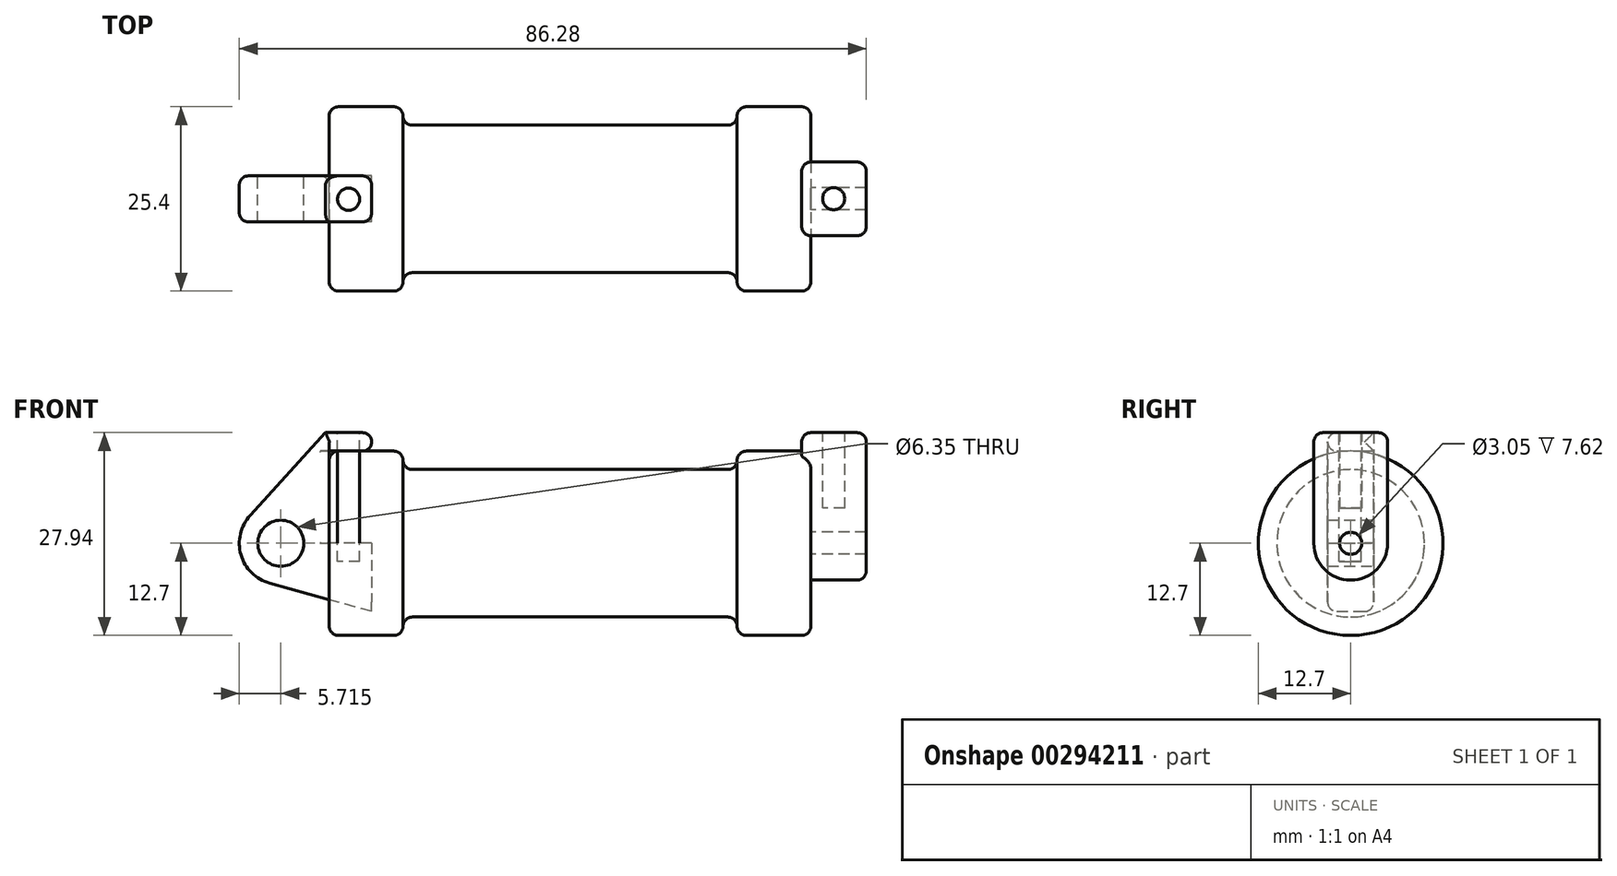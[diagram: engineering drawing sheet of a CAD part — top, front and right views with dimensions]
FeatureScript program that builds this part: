
annotation { "Feature Type Name" : "Feature", "Feature Type Description" : "" }
export const myFeature = defineFeature(function(context is Context, id is Id, definition is map)
    precondition{}
    {
        {
            var Q0;
            Q0=qCreatedBy(makeId("Front.planeOp"),FACE);
            var sketch = newSketch(context, id + "F0", { "sketchPlane" : qUnion([Q0])});
            skLineSegment(sketch, "E0", {"start": v(0, 0) * mm, "end": v(0, 12.7) * mm});
            skLineSegment(sketch, "E1", {"start": v(0, 12.7) * mm, "end": v(10.16, 12.7) * mm});
            skLineSegment(sketch, "E2", {"start": v(10.16, 12.7) * mm, "end": v(10.16, 10.16) * mm});
            skLineSegment(sketch, "E3", {"start": v(10.16, 10.16) * mm, "end": v(56.13, 10.16) * mm});
            skLineSegment(sketch, "E4", {"start": v(56.13, 10.16) * mm, "end": v(56.13, 12.7) * mm});
            skLineSegment(sketch, "E5", {"start": v(56.13, 12.7) * mm, "end": v(66.3, 12.7) * mm});
            skLineSegment(sketch, "E6", {"start": v(66.3, 12.7) * mm, "end": v(66.3, 0) * mm});
            skLineSegment(sketch, "E7", {"start": v(66.3, 0) * mm, "end": v(0, 0) * mm});
            skLineSegment(sketch, "E8", {"start": v(5.84, 15.24) * mm, "end": v(-0.5, 15.24) * mm});
            skLineSegment(sketch, "E9", {"start": v(-0.5, 15.24) * mm, "end": v(-10.88, 3.85) * mm});
            skLineSegment(sketch, "E10", {"start": v(0, 0) * mm, "end": v(-6.65, 0) * mm});
            skCircle(sketch, "E11", {"center": v(-6.65, 0) * mm, "radius": 5.72 * mm});
            skCircle(sketch, "E12", {"center": v(-6.65, 0) * mm, "radius": 3.18 * mm});
            skLineSegment(sketch, "E13", {"start": v(5.84, 15.24) * mm, "end": v(5.84, -9.4) * mm});
            skLineSegment(sketch, "E14", {"start": v(5.84, -9.4) * mm, "end": v(-8.18, -5.5) * mm});
            skSolve(sketch);
        }
        {
            var Q0;
            {var subQ5=sQuery(id+"F0.wireOp",EDGE,"E12");Q0=makeQuery(id+"F0.imprint","IMPRINT",FACE,{"disambiguationData":[TD([[makeQuery(id+"F0.imprint","IMPRINT",EDGE,{"derivedFrom":subQ5}),-1.0]])]});}
            var Q1;
            {var subQ1=sQuery(id+"F0.wireOp",EDGE,"E0");Q1=makeQuery(id+"F0.imprint","IMPRINT",FACE,{"disambiguationData":[TD([[makeQuery(id+"F0.imprint","IMPRINT",EDGE,{"derivedFrom":subQ1}),1.0]])]});}
            var Q2;
            {var subQ0=sQuery(id+"F0.wireOp",EDGE,"E14");Q2=makeQuery(id+"F0.imprint","IMPRINT",FACE,{"disambiguationData":[TD([[makeQuery(id+"F0.imprint","IMPRINT",EDGE,{"derivedFrom":subQ0}),-1.0]])]});}
            extrude(context, id + "F1", {"entities" : qUnion([Q0, Q1, Q2]), "depth" : 3.17 * mm, "hasSecondDirection" : true, "secondDirectionOppositeDirection" : true, "secondDirectionDepth" : 3.17 * mm});
        }
        {
            var Q0;
            {var subQ0=sQuery(id+"F0.wireOp",EDGE,"E0");Q0=makeQuery(id+"F0.imprint","IMPRINT",FACE,{"disambiguationData":[TD([[makeQuery(id+"F0.imprint","IMPRINT",EDGE,{"derivedFrom":subQ0}),-1.0]])]});}
            var Q1;
            {var subQ0=sQuery(id+"F0.wireOp",EDGE,"E2");Q1=makeQuery(id+"F0.imprint","IMPRINT",FACE,{"disambiguationData":[TD([[makeQuery(id+"F0.imprint","IMPRINT",EDGE,{"derivedFrom":subQ0}),-1.0]])]});}
            var Q2;
            Q2=sQuery(id+"F0.wireOp",EDGE,"E7");
            revolve(context, id + "F2", {"entities" : qUnion([Q0, Q1]), "axis" : qUnion([Q2]), "revolveType" : RevolveType.SYMMETRIC, "angle" : 360 * degree});
        }
        {
            var Q0;
            Q0=makeQuery(id+"F2.opRevolve","SWEPT_FACE",FACE,{"disambiguationData":[OSD([sQuery(id+"F0.wireOp",EDGE,"E6")])]});
            var sketch = newSketch(context, id + "F3", { "sketchPlane" : qUnion([Q0])});
            skCircle(sketch, "E15", {"center": v(0, 0) * mm, "radius": 1.52 * mm});
            skCircle(sketch, "E16", {"center": v(0, 0) * mm, "radius": 5.08 * mm});
            skLineSegment(sketch, "E17", {"start": v(-5.08, 0) * mm, "end": v(-5.08, 15.24) * mm});
            skLineSegment(sketch, "E18", {"start": v(5.08, 0) * mm, "end": v(5.08, 15.24) * mm});
            skLineSegment(sketch, "E19", {"start": v(-5.08, 15.24) * mm, "end": v(5.08, 15.24) * mm});
            skSolve(sketch);
        }
        {
            var Q0;
            {var subQ0=sQuery(id+"F3.wireOp",EDGE,"E17");var subQ1=sQuery(id+"F3.wireOp",EDGE,"E16");var subQ2=makeQuery(id+"F3.imprint","INTERSECT",VERTEX,{"derivedFrom":[subQ1,subQ0]});Q0=makeQuery(id+"F3.imprint","IMPRINT",FACE,{"disambiguationData":[TD([[makeQuery(id+"F3.imprint","IMPRINT",EDGE,{"disambiguationData":[TD([[subQ2,1.0]])],"derivedFrom":subQ1}),-1.0]])]});}
            var Q1;
            Q1=makeQuery(id+"F3.imprint","IMPRINT",FACE,{"disambiguationData":[TD([[makeQuery(id+"F3.imprint","IMPRINT",EDGE,{"derivedFrom":sQuery(id+"F3.wireOp",EDGE,"E15")}),-1.0]])]});
            var Q2;
            {var subQ0=sQuery(id+"F3.wireOp",EDGE,"E19");Q2=makeQuery(id+"F3.imprint","IMPRINT",FACE,{"disambiguationData":[TD([[makeQuery(id+"F3.imprint","IMPRINT",EDGE,{"derivedFrom":subQ0}),-1.0]])]});}
            extrude(context, id + "F4", {"entities" : qUnion([Q0, Q1, Q2]), "operationType" : NewBodyOperationType.ADD, "depth" : 7.62 * mm});
        }
        {
            var Q0;
            Q0=makeQuery(id+"F4.opExtrude","CAP_FACE",FACE,{"disambiguationData":[OSD([sQuery(id+"F3.wireOp",EDGE,"E15"),sQuery(id+"F3.wireOp",EDGE,"E16"),sQuery(id+"F3.wireOp",EDGE,"E17"),sQuery(id+"F3.wireOp",EDGE,"E18"),sQuery(id+"F3.wireOp",EDGE,"E19")])],"isStart":true});
            extrude(context, id + "F5", {"entities" : qUnion([Q0]), "operationType" : NewBodyOperationType.ADD, "depth" : 1.27 * mm});
        }
        {
            var Q0;
            Q0=makeQuery(id+"F1.opExtrude","SWEPT_FACE",FACE,{"disambiguationData":[OSD([sQuery(id+"F0.wireOp",EDGE,"E8")])]});
            var sketch = newSketch(context, id + "F6", { "sketchPlane" : qUnion([Q0])});
            skCircle(sketch, "E20", {"center": v(2.67, -0.04) * mm, "radius": 1.52 * mm});
            skSolve(sketch);
        }
        {
            var Q0;
            {var subQ0=sQuery(id+"F3.wireOp",EDGE,"E19");Q0=makeQuery(id+"F5.boolean.opBoolean","MERGE",FACE,{"derivedFrom":[makeQuery(id+"F4.opExtrude","SWEPT_FACE",FACE,{"disambiguationData":[OSD([subQ0])]}),makeQuery(id+"F5.opExtrude","SWEPT_FACE",FACE,{"disambiguationData":[OSD([subQ0])]})]});}
            var sketch = newSketch(context, id + "F7", { "sketchPlane" : qUnion([Q0])});
            skCircle(sketch, "E21", {"center": v(69.43, 0.04) * mm, "radius": 1.52 * mm});
            skSolve(sketch);
        }
        {
            var Q0;
            Q0=makeQuery(id+"F6.imprint","IMPRINT",FACE,{"disambiguationData":[TD([[makeQuery(id+"F6.imprint","IMPRINT",EDGE,{"derivedFrom":sQuery(id+"F6.wireOp",EDGE,"E20")}),1.0]])]});
            var Q1;
            Q1=sQuery(id+"F6.wireOp",EDGE,"E20");
            extrude(context, id + "F8", {"entities" : qUnion([Q0]), "surfaceEntities" : qUnion([Q1]), "oppositeDirection" : true, "depth" : 17.78 * mm});
        }
        {
            var Q0;
            Q0=makeQuery(id+"F7.imprint","IMPRINT",FACE,{"disambiguationData":[TD([[makeQuery(id+"F7.imprint","IMPRINT",EDGE,{"derivedFrom":sQuery(id+"F7.wireOp",EDGE,"E21")}),1.0]])]});
            var Q1;
            Q1=sQuery(id+"F7.wireOp",EDGE,"E21");
            extrude(context, id + "F9", {"entities" : qUnion([Q0]), "surfaceEntities" : qUnion([Q1]), "oppositeDirection" : true, "depth" : 10.4 * mm});
        }
        {
            var Q0;
            Q0=makeQuery(id+"F2.opRevolve","SWEPT_FACE",FACE,{"disambiguationData":[OSD([sQuery(id+"F0.wireOp",EDGE,"E2")])]});
            var Q1;
            Q1=makeQuery(id+"F2.opRevolve","SWEPT_EDGE",EDGE,{"disambiguationData":[OSD([sQuery(id+"F0.wireOp",EDGE,"E4"),sQuery(id+"F0.wireOp",EDGE,"E5")])]});
            var Q2;
            Q2=makeQuery(id+"F2.opRevolve","SWEPT_FACE",FACE,{"disambiguationData":[OSD([sQuery(id+"F0.wireOp",EDGE,"E3")])]});
            var Q3;
            {var subQ0=sQuery(id+"F0.wireOp",EDGE,"E13");Q3=makeQuery(id+"F1.opExtrude","SWEPT_FACE",FACE,{"disambiguationData":[OSD([subQ0]),TDD([makeQuery(id+"F0.imprint","IMPRINT",EDGE,{"disambiguationData":[TD([[makeQuery(id+"F0.imprint","INTERSECT",VERTEX,{"derivedFrom":[sQuery(id+"F0.wireOp",EDGE,"E8"),subQ0]}),-1.0]])],"derivedFrom":subQ0})])]});}
            var Q4;
            Q4=makeQuery(id+"F2.opRevolve","SWEPT_FACE",FACE,{"disambiguationData":[OSD([sQuery(id+"F0.wireOp",EDGE,"E1")])]});
            var Q5;
            Q5=makeQuery(id+"F1.opExtrude","CAP_EDGE",EDGE,{"disambiguationData":[OSD([sQuery(id+"F0.wireOp",EDGE,"E11")])],"isStart":false});
            var Q6;
            Q6=makeQuery(id+"F1.opExtrude","CAP_EDGE",EDGE,{"disambiguationData":[OSD([sQuery(id+"F0.wireOp",EDGE,"E9")])],"isStart":false});
            var Q7;
            Q7=makeQuery(id+"F1.opExtrude","CAP_EDGE",EDGE,{"disambiguationData":[OSD([sQuery(id+"F0.wireOp",EDGE,"E8")])],"isStart":false});
            var Q8;
            Q8=makeQuery(id+"F1.opExtrude","CAP_EDGE",EDGE,{"disambiguationData":[OSD([sQuery(id+"F0.wireOp",EDGE,"E0")])],"isStart":true});
            fillet(context, id + "F10", {"entities" : qUnion([Q0, Q1, Q2, Q3, Q4, Q5, Q6, Q7, Q8]), "radius" : 1.27 * mm, "tangentPropagation" : true, "allowEdgeOverflow" : false});
        }
        {
            var Q0;
            {var subQ0=sQuery(id+"F0.wireOp",EDGE,"E5");var subQ1=sQuery(id+"F0.wireOp",EDGE,"E6");Q0=makeQuery(id+"F4.boolean.opBoolean","SPLIT",EDGE,{"disambiguationData":[topologyDisambiguationEdgeConnected([makeQuery(id+"F2.opRevolve","SWEPT_FACE",FACE,{"disambiguationData":[OSD([subQ1])]})])],"derivedFrom":makeQuery(id+"F2.opRevolve","SWEPT_EDGE",EDGE,{"disambiguationData":[OSD([subQ0,subQ1])]})});}
            var Q1;
            Q1=makeQuery(id+"F5.opExtrude","CAP_EDGE",EDGE,{"disambiguationData":[OSD([sQuery(id+"F3.wireOp",EDGE,"E19")])],"isStart":false});
            var Q2;
            {var subQ0=sQuery(id+"F3.wireOp",EDGE,"E19");var subQ1=sQuery(id+"F3.wireOp",EDGE,"E17");Q2=makeQuery(id+"F5.boolean.opBoolean","MERGE",EDGE,{"derivedFrom":[makeQuery(id+"F4.opExtrude","SWEPT_EDGE",EDGE,{"disambiguationData":[OSD([subQ1,subQ0])]}),makeQuery(id+"F5.opExtrude","SWEPT_EDGE",EDGE,{"disambiguationData":[OSD([subQ1,subQ0])]})]});}
            var Q3;
            Q3=makeQuery(id+"F4.opExtrude","CAP_EDGE",EDGE,{"disambiguationData":[OSD([sQuery(id+"F3.wireOp",EDGE,"E19")])],"isStart":false});
            var Q4;
            {var subQ0=sQuery(id+"F3.wireOp",EDGE,"E19");var subQ1=sQuery(id+"F3.wireOp",EDGE,"E18");Q4=makeQuery(id+"F5.boolean.opBoolean","MERGE",EDGE,{"derivedFrom":[makeQuery(id+"F4.opExtrude","SWEPT_EDGE",EDGE,{"disambiguationData":[OSD([subQ1,subQ0])]}),makeQuery(id+"F5.opExtrude","SWEPT_EDGE",EDGE,{"disambiguationData":[OSD([subQ1,subQ0])]})]});}
            var Q5;
            Q5=makeQuery(id+"F4.opExtrude","CAP_EDGE",EDGE,{"disambiguationData":[OSD([sQuery(id+"F3.wireOp",EDGE,"E17")])],"isStart":false});
            fillet(context, id + "F11", {"entities" : qUnion([Q0, Q1, Q2, Q3, Q4, Q5]), "radius" : 1.27 * mm, "tangentPropagation" : true, "allowEdgeOverflow" : false});
        }
        {
            var Q0;
            Q0=makeQuery(id+"F5.opExtrude","CAP_EDGE",EDGE,{"disambiguationData":[OSD([sQuery(id+"F3.wireOp",EDGE,"E18")])],"isStart":false});
            var Q1;
            Q1=makeQuery(id+"F5.opExtrude","CAP_EDGE",EDGE,{"disambiguationData":[OSD([sQuery(id+"F3.wireOp",EDGE,"E17")])],"isStart":false});
            fillet(context, id + "F12", {"entities" : qUnion([Q0, Q1]), "radius" : 1.27 * mm, "tangentPropagation" : true, "allowEdgeOverflow" : false});
        }
        {
            var Q0;
            Q0=makeQuery(id+"F5.opExtrude","CAP_EDGE",EDGE,{"disambiguationData":[OSD([sQuery(id+"F0.wireOp",EDGE,"E5"),sQuery(id+"F0.wireOp",EDGE,"E6")])],"isStart":false});
            var Q1;
            Q1=makeQuery(id+"F1.opExtrude","CAP_EDGE",EDGE,{"disambiguationData":[OSD([sQuery(id+"F0.wireOp",EDGE,"E1")])],"isStart":false});
            fillet(context, id + "F13", {"entities" : qUnion([Q0, Q1]), "radius" : 1.27 * mm, "tangentPropagation" : true, "allowEdgeOverflow" : false});
        }
        {
            var Q0;
            Q0=makeQuery(id+"F1.opExtrude","CAP_EDGE",EDGE,{"disambiguationData":[OSD([sQuery(id+"F0.wireOp",EDGE,"E9")])],"isStart":true});
            var Q1;
            {var subQ0=sQuery(id+"F0.wireOp",EDGE,"E9");Q1=makeQuery(id+"F10.opFillet","BLEND_EDGE",EDGE,{"blendedFrom":[makeQuery(id+"F1.opExtrude","CAP_EDGE",EDGE,{"disambiguationData":[OSD([subQ0])],"isStart":false}),makeQuery(id+"F1.opExtrude","SWEPT_FACE",FACE,{"disambiguationData":[OSD([subQ0])]})],"blendedInto":[makeQuery(id+"F1.opExtrude","SWEPT_FACE",FACE,{"disambiguationData":[OSD([subQ0])]})]});}
            fillet(context, id + "F14", {"entities" : qUnion([Q0, Q1]), "radius" : 1.27 * mm, "tangentPropagation" : true, "allowEdgeOverflow" : false});
        }
    });
